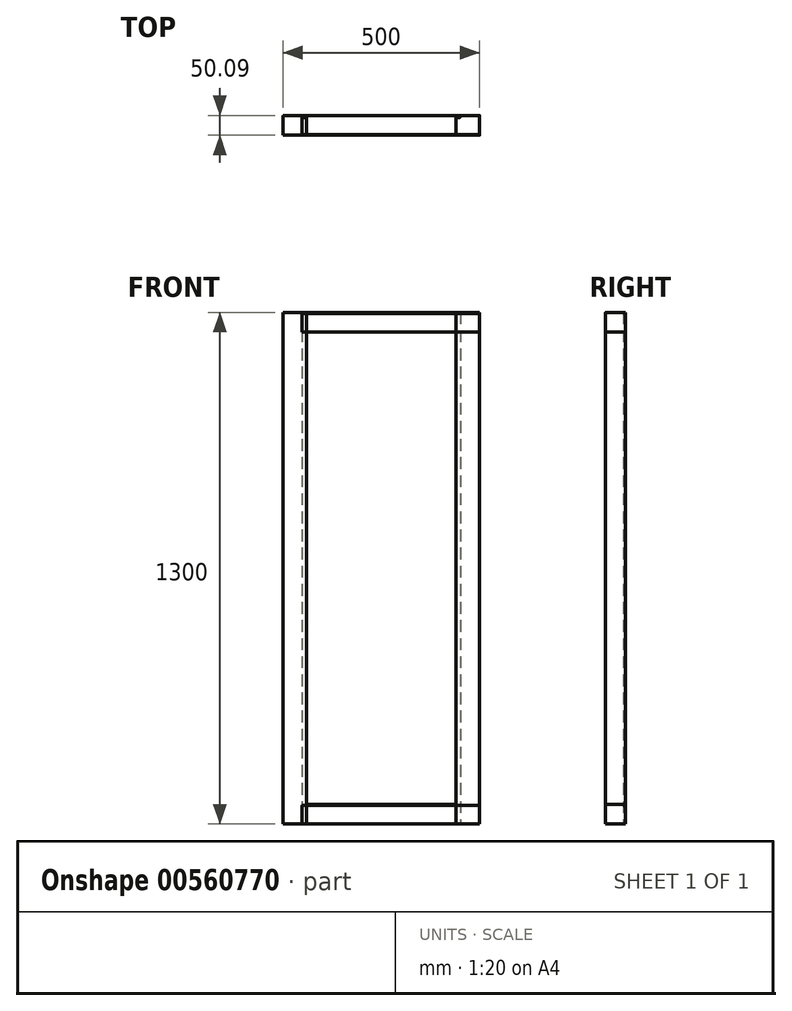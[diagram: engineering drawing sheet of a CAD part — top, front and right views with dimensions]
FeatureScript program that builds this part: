
annotation { "Feature Type Name" : "Feature", "Feature Type Description" : "" }
export const myFeature = defineFeature(function(context is Context, id is Id, definition is map)
    precondition{}
    {
        {
            var Q0;
            Q0=qCreatedBy(makeId("Top.planeOp"),FACE);
            var sketch = newSketch(context, id + "F0", { "sketchPlane" : qUnion([Q0])});
            skLineSegment(sketch, "E0", {"start": v(-60, 0) * mm, "end": v(-60, 43) * mm});
            skLineSegment(sketch, "E1", {"start": v(-58, 45) * mm, "end": v(-51, 45) * mm});
            skLineSegment(sketch, "E2", {"start": v(-49, 47) * mm, "end": v(-49, 48) * mm});
            skLineSegment(sketch, "E3", {"start": v(-47, 50) * mm, "end": v(-2, 50) * mm});
            skLineSegment(sketch, "E4", {"start": v(0, 48) * mm, "end": v(0, 0) * mm});
            skLineSegment(sketch, "E5", {"start": v(0, 0) * mm, "end": v(-60, 0) * mm});
            skPoint(sketch, "E6.visualSharp", {"position": v(-60, 45) * mm});
            skArc(sketch, "E6.filletArc", {"start": v(-58, 45) * mm, "mid": v(-59.41, 44.41) * mm, "end": v(-60, 43) * mm});
            skPoint(sketch, "E7.visualSharp", {"position": v(-49, 50) * mm});
            skArc(sketch, "E7.filletArc", {"start": v(-47, 50) * mm, "mid": v(-48.41, 49.41) * mm, "end": v(-49, 48) * mm});
            skPoint(sketch, "E8.visualSharp", {"position": v(0, 50) * mm});
            skArc(sketch, "E8.filletArc", {"start": v(0, 48) * mm, "mid": v(-0.59, 49.41) * mm, "end": v(-2, 50) * mm});
            skPoint(sketch, "E9.visualSharp", {"position": v(-49, 45) * mm});
            skArc(sketch, "E9.filletArc", {"start": v(-51, 45) * mm, "mid": v(-49.59, 45.59) * mm, "end": v(-49, 47) * mm});
            skSolve(sketch);
        }
        {
            var Q0;
            Q0=qCreatedBy(makeId("Right.planeOp"),FACE);
            var sketch = newSketch(context, id + "F1", { "sketchPlane" : qUnion([Q0])});
            skArc(sketch, "E10.MirrorCS", {"start": v(0, 47.4) * mm, "mid": v(0.32, 49.22) * mm, "end": v(2, 50) * mm});
            skLineSegment(sketch, "E11.MirrorCS", {"start": v(43.53, 50) * mm, "end": v(2, 50) * mm});
            skLineSegment(sketch, "E12.MirrorCS", {"start": v(50, 0) * mm, "end": v(50, 41.61) * mm});
            skLineSegment(sketch, "E13.MirrorCS", {"start": v(0, 0) * mm, "end": v(50, 0) * mm});
            skLineSegment(sketch, "E14.MirrorCS", {"start": v(0, 47.4) * mm, "end": v(0, 0) * mm});
            skLineSegment(sketch, "E15", {"start": v(45.17, 49.15) * mm, "end": v(49.64, 42.76) * mm});
            skPoint(sketch, "E16.visualSharp", {"position": v(44.57, 50) * mm});
            skArc(sketch, "E16.filletArc", {"start": v(45.17, 49.15) * mm, "mid": v(44.45, 49.77) * mm, "end": v(43.53, 50) * mm});
            skPoint(sketch, "E17.visualSharp", {"position": v(50, 42.24) * mm});
            skArc(sketch, "E17.filletArc", {"start": v(50, 41.61) * mm, "mid": v(49.9, 42.21) * mm, "end": v(49.64, 42.76) * mm});
            skSolve(sketch);
        }
        {
            var Q0;
            Q0 = qSketchRegion(id + "F0", true);
            extrude(context, id + "F2", {"entities" : qUnion([Q0]), "depth" : 1300 * mm, "offsetDistance" : 25 * mm});
        }
        {
            var Q0;
            Q0=qCreatedBy(makeId("Right.planeOp"),FACE);
            cPlane(context, id + "F3", {"entities" : qUnion([Q0]), "cplaneType" : CPlaneType.OFFSET, "offset" : 250 * mm, "oppositeDirection" : true, "width" : 150 * mm, "height" : 150 * mm});
        }
        {
            var Q0;
            Q0=makeQuery(id+"F2.opExtrude","SWEPT_BODY",BODY,{"disambiguationData":[OSD([sQuery(id+"F0.wireOp",EDGE,"E0"),sQuery(id+"F0.wireOp",EDGE,"E1"),sQuery(id+"F0.wireOp",EDGE,"E2"),sQuery(id+"F0.wireOp",EDGE,"E3"),sQuery(id+"F0.wireOp",EDGE,"E4"),sQuery(id+"F0.wireOp",EDGE,"E5"),sQuery(id+"F0.wireOp",EDGE,"E6.filletArc"),sQuery(id+"F0.wireOp",EDGE,"E7.filletArc"),sQuery(id+"F0.wireOp",EDGE,"E8.filletArc"),sQuery(id+"F0.wireOp",EDGE,"E9.filletArc")])]});
            var Q1;
            Q1=qCreatedBy(id+"F3.planeOp",FACE);
            mirror(context, id + "F4", {"entities" : qUnion([Q0]), "mirrorPlane" : qUnion([Q1])});
        }
        {
            var Q0;
            Q0 = qSketchRegion(id + "F1", true);
            extrude(context, id + "F5", {"entities" : qUnion([Q0]), "oppositeDirection" : true, "depth" : 451 * mm, "offsetDistance" : 25 * mm});
        }
        {
            var Q0;
            Q0=makeQuery(id+"F5.opExtrude","SWEPT_BODY",BODY,{"disambiguationData":[OSD([sQuery(id+"F1.wireOp",EDGE,"E10.MirrorCS"),sQuery(id+"F1.wireOp",EDGE,"E11.MirrorCS"),sQuery(id+"F1.wireOp",EDGE,"E12.MirrorCS"),sQuery(id+"F1.wireOp",EDGE,"E13.MirrorCS"),sQuery(id+"F1.wireOp",EDGE,"E14.MirrorCS"),sQuery(id+"F1.wireOp",EDGE,"E15"),sQuery(id+"F1.wireOp",EDGE,"E16.filletArc"),sQuery(id+"F1.wireOp",EDGE,"E17.filletArc")])]});
            transform(context, id + "F6", {"entities" : qUnion([Q0]), "transformType" : TransformType.TRANSLATION_3D, "dx" : 0 * mm, "dy" : 0 * mm, "dz" : 1250 * mm, "makeCopy" : true});
        }
    });
